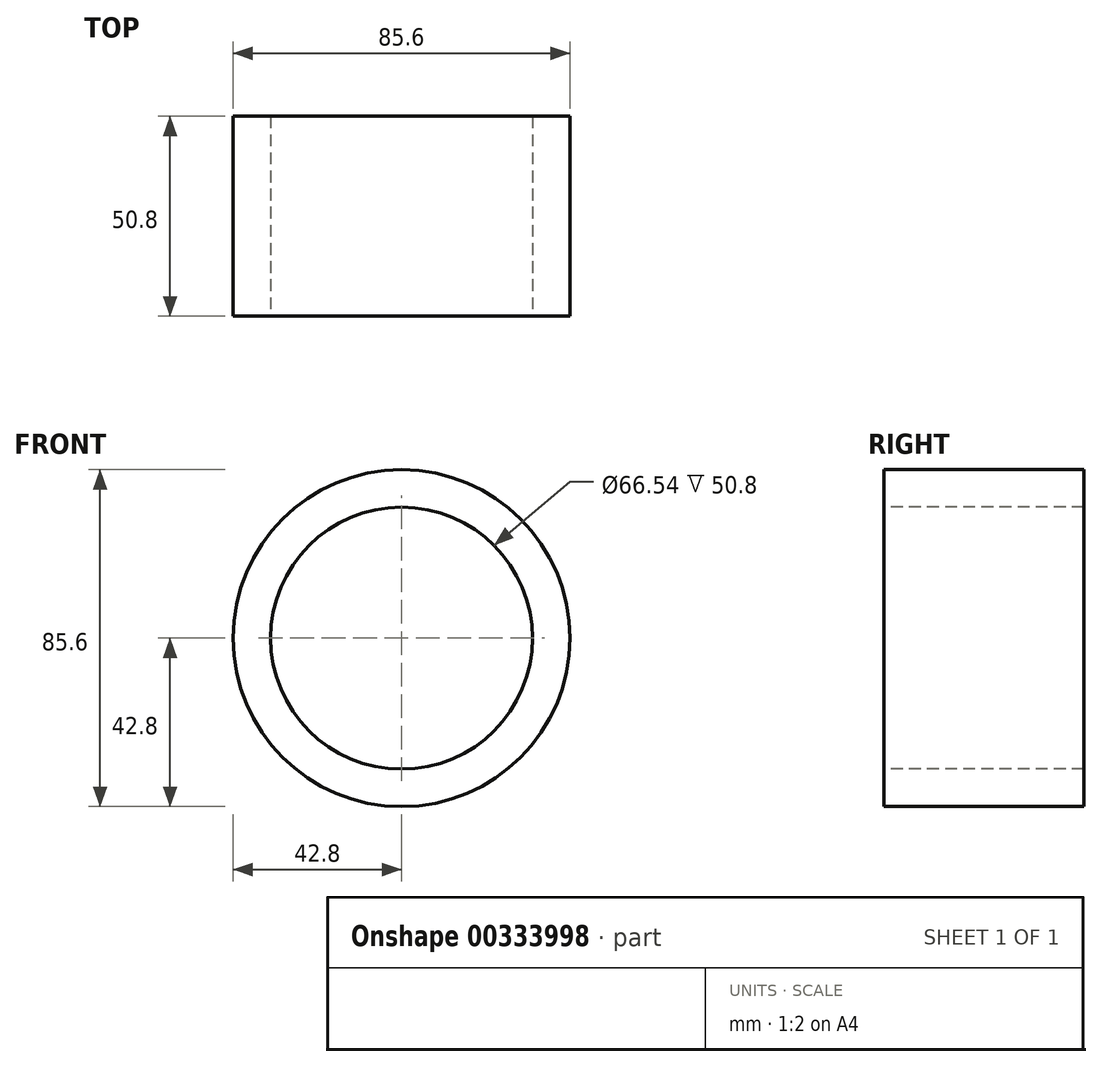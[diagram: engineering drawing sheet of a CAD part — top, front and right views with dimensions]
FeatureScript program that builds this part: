
annotation { "Feature Type Name" : "Feature", "Feature Type Description" : "" }
export const myFeature = defineFeature(function(context is Context, id is Id, definition is map)
    precondition{}
    {
        {
            var Q0;
            Q0=qCreatedBy(makeId("Front.planeOp"),FACE);
            var sketch = newSketch(context, id + "F0", { "sketchPlane" : qUnion([Q0])});
            skCircle(sketch, "E0", {"center": v(0, 0) * mm, "radius": 33.27 * mm});
            skCircle(sketch, "E1.0", {"center": v(0, 0) * mm, "radius": 42.8 * mm});
            skLineSegment(sketch, "E2", {"start": v(-42.8, 0) * mm, "end": v(-42.8, 50.37) * mm});
            skLineSegment(sketch, "E3", {"start": v(-42.8, 50.37) * mm, "end": v(92.78, 50.37) * mm});
            skLineSegment(sketch, "E4", {"start": v(92.78, 50.37) * mm, "end": v(92.78, -18.32) * mm});
            skLineSegment(sketch, "E5", {"start": v(92.78, -18.32) * mm, "end": v(38.68, -18.32) * mm});
            skLineSegment(sketch, "E6.0", {"start": v(92.78, 26.13) * mm, "end": v(38.68, 26.13) * mm});
            skSolve(sketch);
        }
        {
            var Q0;
            Q0=qCreatedBy(makeId("Front.planeOp"),FACE);
            var sketch = newSketch(context, id + "F1", { "sketchPlane" : qUnion([Q0])});
            skSolve(sketch);
        }
        {
            var Q0;
            Q0 = qSketchRegion(id + "F1", true);
            var Q1;
            Q1=makeQuery(id+"F0.imprint","IMPRINT",FACE,{"disambiguationData":[TD([[makeQuery(id+"F0.imprint","IMPRINT",EDGE,{"derivedFrom":sQuery(id+"F0.wireOp",EDGE,"E0")}),-1.0]])]});
            extrude(context, id + "F2", {"entities" : qUnion([Q0, Q1]), "oppositeDirection" : true, "depth" : 50.8 * mm});
        }
    });
